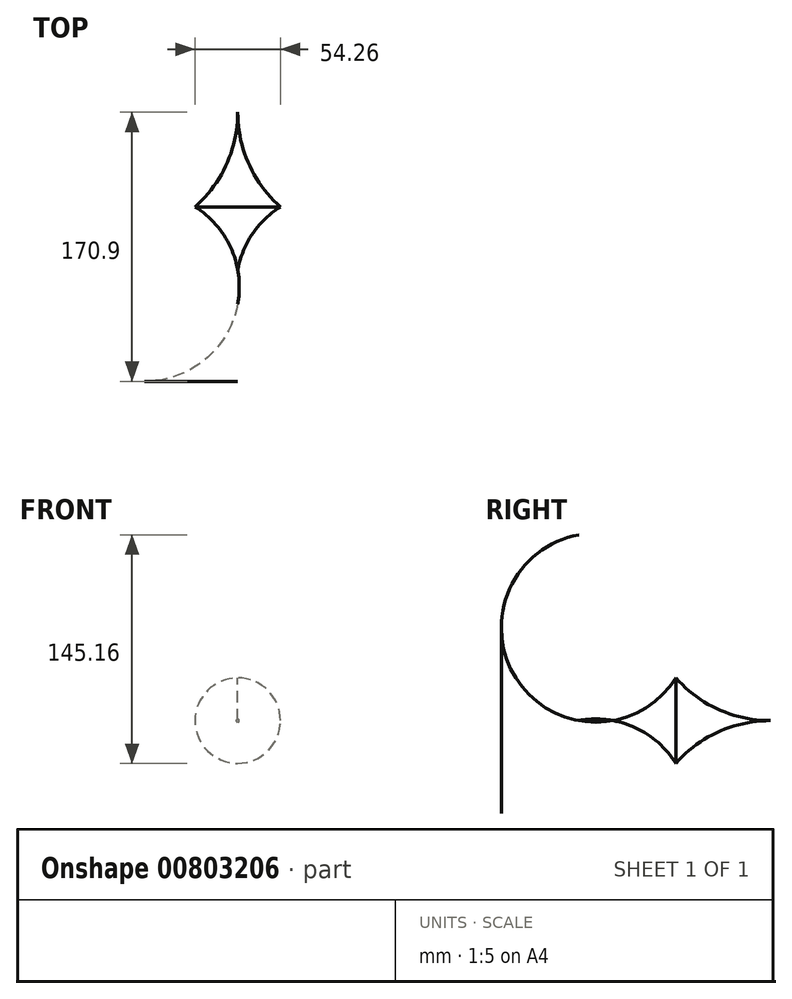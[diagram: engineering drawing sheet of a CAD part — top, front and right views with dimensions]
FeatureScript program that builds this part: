
annotation { "Feature Type Name" : "Feature", "Feature Type Description" : "" }
export const myFeature = defineFeature(function(context is Context, id is Id, definition is map)
    precondition{}
    {
        {
            var Q0;
            Q0=qCreatedBy(makeId("Top.planeOp"),FACE);
            var sketch = newSketch(context, id + "F0", { "sketchPlane" : qUnion([Q0])});
            skLineSegment(sketch, "E0", {"start": v(0, 74.51) * mm, "end": v(0, -71.08) * mm, "construction": true});
            skArc(sketch, "E1", {"start": v(27.13, 0) * mm, "mid": v(9.36, -17.15) * mm, "end": v(0, -40) * mm});
            skArc(sketch, "E2", {"start": v(0, 60) * mm, "mid": v(7.1, 27.08) * mm, "end": v(27.13, 0) * mm});
            skLineSegment(sketch, "E3", {"start": v(0, 60) * mm, "end": v(0, -40) * mm});
            skSolve(sketch);
        }
        {
            var Q0;
            Q0=makeQuery(id+"F0.imprint","IMPRINT",FACE,{"disambiguationData":[TD([[makeQuery(id+"F0.imprint","IMPRINT",EDGE,{"derivedFrom":sQuery(id+"F0.wireOp",EDGE,"E1")}),-1.0]])]});
            var Q1;
            Q1=sQuery(id+"F0.wireOp",EDGE,"E0");
            revolve(context, id + "F1", {"surfaceOperationType" : NewSurfaceOperationType.NEW, "entities" : qUnion([Q0]), "axis" : qUnion([Q1]), "revolveType" : RevolveType.FULL});
        }
    });
